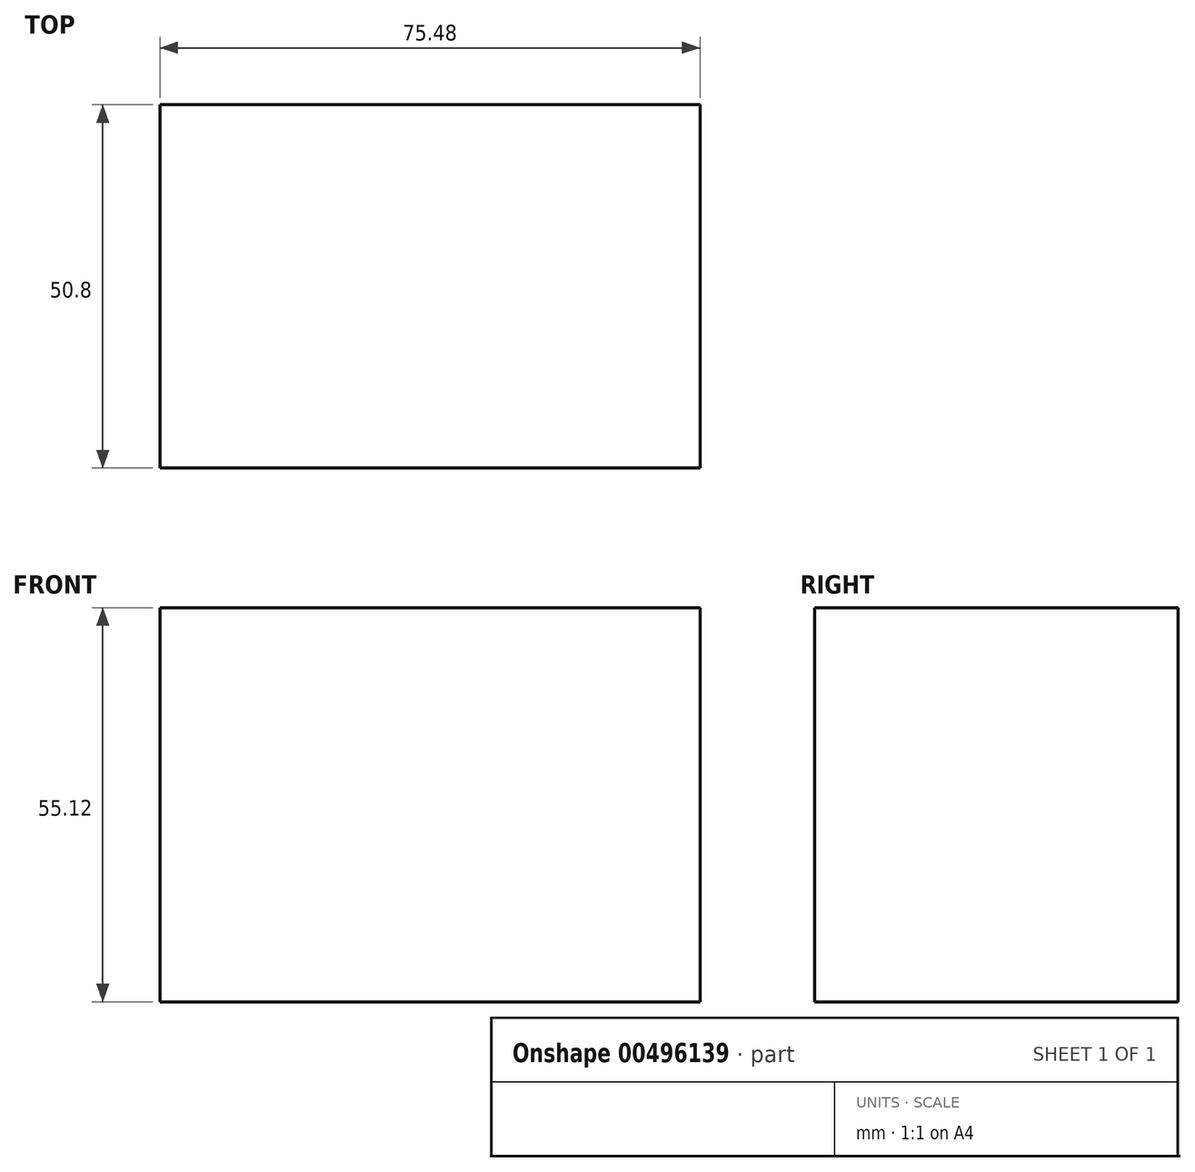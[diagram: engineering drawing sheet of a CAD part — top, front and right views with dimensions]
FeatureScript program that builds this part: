
annotation { "Feature Type Name" : "Feature", "Feature Type Description" : "" }
export const myFeature = defineFeature(function(context is Context, id is Id, definition is map)
    precondition{}
    {
        {
            var Q0;
            Q0=qCreatedBy(makeId("Front.planeOp"),FACE);
            var sketch = newSketch(context, id + "F0", { "sketchPlane" : qUnion([Q0])});
            skLineSegment(sketch, "E0.bottom", {"start": v(-58.4, 42.1) * mm, "end": v(17.08, 42.1) * mm});
            skLineSegment(sketch, "E0.top", {"start": v(-58.4, -13.02) * mm, "end": v(17.08, -13.02) * mm});
            skLineSegment(sketch, "E0.left", {"start": v(-58.4, 42.1) * mm, "end": v(-58.4, -13.02) * mm});
            skLineSegment(sketch, "E0.right", {"start": v(17.08, 42.1) * mm, "end": v(17.08, -13.02) * mm});
            skSolve(sketch);
        }
        {
            var Q0;
            Q0=makeQuery(id+"F0.imprint","IMPRINT",FACE,{"disambiguationData":[TD([[makeQuery(id+"F0.imprint","IMPRINT",EDGE,{"derivedFrom":sQuery(id+"F0.wireOp",EDGE,"E0.bottom")}),-1.0]])]});
            extrude(context, id + "F1", {"entities" : qUnion([Q0]), "oppositeDirection" : true, "depth" : 50.8 * mm});
        }
    });
